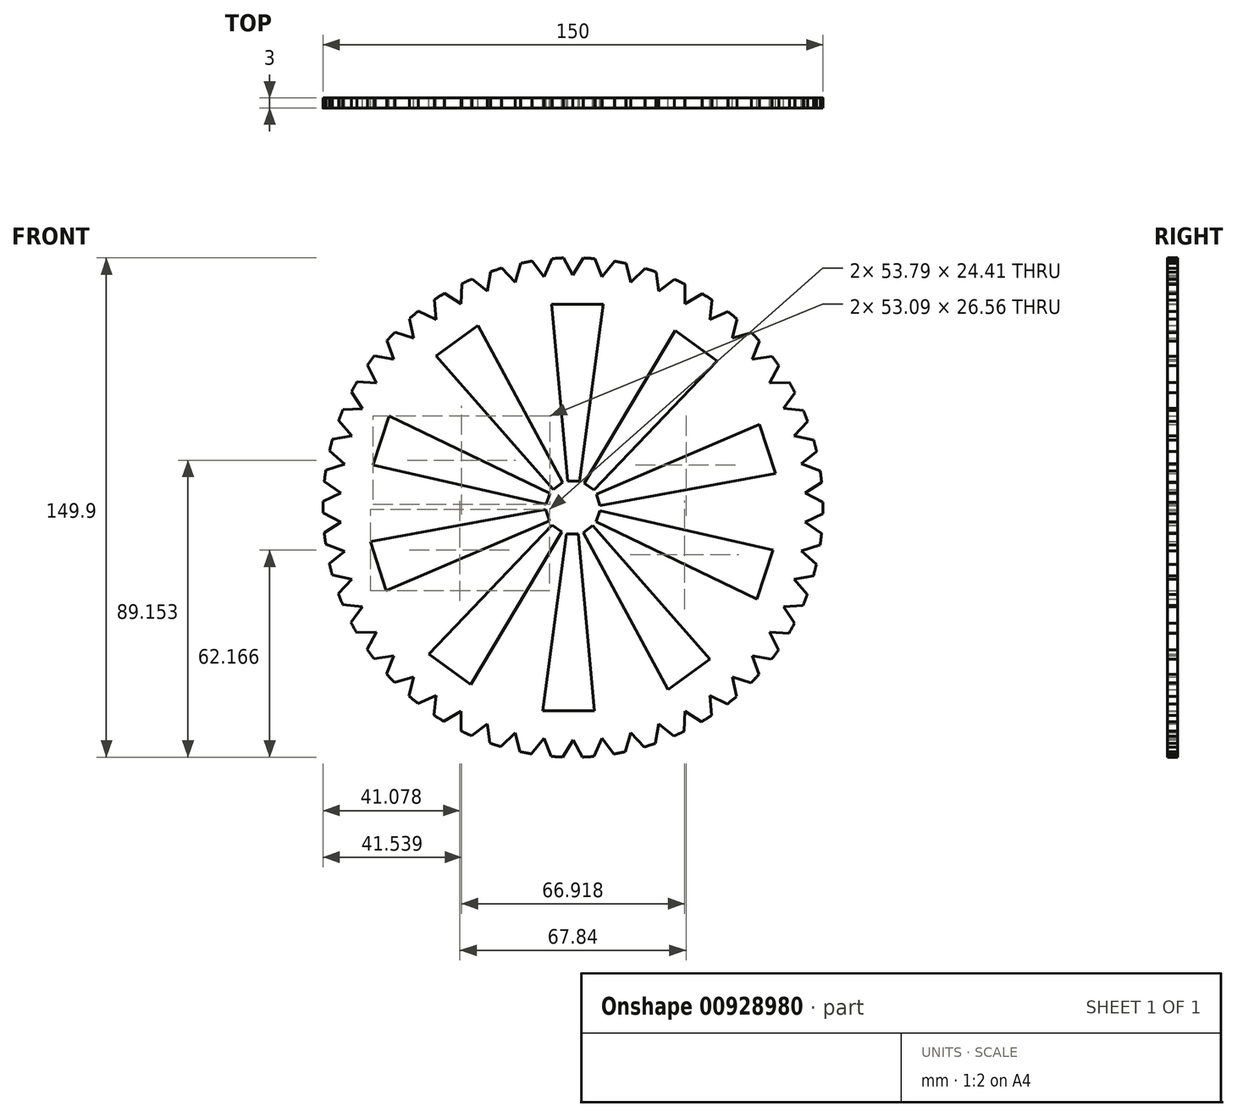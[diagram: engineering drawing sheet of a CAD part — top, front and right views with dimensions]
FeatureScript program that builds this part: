
annotation { "Feature Type Name" : "Feature", "Feature Type Description" : "" }
export const myFeature = defineFeature(function(context is Context, id is Id, definition is map)
    precondition{}
    {
        {
            var Q0;
            Q0=qCreatedBy(makeId("Front.planeOp"),FACE);
            var sketch = newSketch(context, id + "F0", { "sketchPlane" : qUnion([Q0])});
            skCircle(sketch, "E0", {"center": v(-17.07, 14.18) * mm, "radius": 75 * mm});
            skCircle(sketch, "E1.cCircle", {"center": v(-16.99, 88.46) * mm, "radius": 2.24 * mm, "construction": true});
            skLineSegment(sketch, "E1.0", {"start": v(-13.07, 90.62) * mm, "end": v(-17.08, 83.99) * mm});
            skLineSegment(sketch, "E1.1", {"start": v(-17.08, 83.99) * mm, "end": v(-20.82, 90.77) * mm});
            skLineSegment(sketch, "E1.2", {"start": v(-20.82, 90.77) * mm, "end": v(-13.07, 90.62) * mm});
            skPoint(sketch, "E1.0.midPoint", {"position": v(-15.07, 87.3) * mm});
            skPoint(sketch, "E2.1.0", {"position": v(-24.25, 86.98) * mm});
            skLineSegment(sketch, "E2.1.1", {"start": v(-30.39, 89.7) * mm, "end": v(-22.68, 90.52) * mm});
            skCircle(sketch, "E2.1.2", {"center": v(-26.3, 87.88) * mm, "radius": 2.24 * mm, "construction": true});
            skLineSegment(sketch, "E2.1.3", {"start": v(-22.68, 90.52) * mm, "end": v(-25.83, 83.43) * mm});
            skLineSegment(sketch, "E2.1.4", {"start": v(-25.83, 83.43) * mm, "end": v(-30.39, 89.7) * mm});
            skPoint(sketch, "E2.2.0", {"position": v(-33.32, 85.5) * mm});
            skLineSegment(sketch, "E2.2.1", {"start": v(-39.75, 87.44) * mm, "end": v(-32.2, 89.21) * mm});
            skCircle(sketch, "E2.2.2", {"center": v(-35.46, 86.15) * mm, "radius": 2.24 * mm, "construction": true});
            skLineSegment(sketch, "E2.2.3", {"start": v(-32.2, 89.21) * mm, "end": v(-34.44, 81.8) * mm});
            skLineSegment(sketch, "E2.2.4", {"start": v(-34.44, 81.8) * mm, "end": v(-39.75, 87.44) * mm});
            skPoint(sketch, "E2.3.0", {"position": v(-42.13, 82.9) * mm});
            skLineSegment(sketch, "E2.3.1", {"start": v(-48.75, 84.02) * mm, "end": v(-41.49, 86.73) * mm});
            skCircle(sketch, "E2.3.2", {"center": v(-44.34, 83.27) * mm, "radius": 2.24 * mm, "construction": true});
            skLineSegment(sketch, "E2.3.3", {"start": v(-41.49, 86.73) * mm, "end": v(-42.77, 79.08) * mm});
            skLineSegment(sketch, "E2.3.4", {"start": v(-42.77, 79.08) * mm, "end": v(-48.75, 84.02) * mm});
            skPoint(sketch, "E2.4.0", {"position": v(-50.55, 79.22) * mm});
            skLineSegment(sketch, "E2.4.1", {"start": v(-57.25, 79.5) * mm, "end": v(-50.39, 83.1) * mm});
            skCircle(sketch, "E2.4.2", {"center": v(-52.78, 79.31) * mm, "radius": 2.24 * mm, "construction": true});
            skLineSegment(sketch, "E2.4.3", {"start": v(-50.39, 83.1) * mm, "end": v(-50.7, 75.35) * mm});
            skLineSegment(sketch, "E2.4.4", {"start": v(-50.7, 75.35) * mm, "end": v(-57.25, 79.5) * mm});
            skPoint(sketch, "E2.5.0", {"position": v(-58.43, 74.51) * mm});
            skLineSegment(sketch, "E2.5.1", {"start": v(-65.12, 73.94) * mm, "end": v(-58.76, 78.37) * mm});
            skCircle(sketch, "E2.5.2", {"center": v(-60.66, 74.32) * mm, "radius": 2.24 * mm, "construction": true});
            skLineSegment(sketch, "E2.5.3", {"start": v(-58.76, 78.37) * mm, "end": v(-58.1, 70.65) * mm});
            skLineSegment(sketch, "E2.5.4", {"start": v(-58.1, 70.65) * mm, "end": v(-65.12, 73.94) * mm});
            skPoint(sketch, "E2.6.0", {"position": v(-65.67, 68.85) * mm});
            skLineSegment(sketch, "E2.6.1", {"start": v(-72.24, 67.45) * mm, "end": v(-66.48, 72.64) * mm});
            skCircle(sketch, "E2.6.2", {"center": v(-67.86, 68.38) * mm, "radius": 2.24 * mm, "construction": true});
            skLineSegment(sketch, "E2.6.3", {"start": v(-66.48, 72.64) * mm, "end": v(-64.86, 65.06) * mm});
            skLineSegment(sketch, "E2.6.4", {"start": v(-64.86, 65.06) * mm, "end": v(-72.24, 67.45) * mm});
            skPoint(sketch, "E2.7.0", {"position": v(-72.14, 62.33) * mm});
            skLineSegment(sketch, "E2.7.1", {"start": v(-78.48, 60.12) * mm, "end": v(-73.42, 65.99) * mm});
            skCircle(sketch, "E2.7.2", {"center": v(-74.25, 61.6) * mm, "radius": 2.24 * mm, "construction": true});
            skLineSegment(sketch, "E2.7.3", {"start": v(-73.42, 65.99) * mm, "end": v(-70.86, 58.67) * mm});
            skLineSegment(sketch, "E2.7.4", {"start": v(-70.86, 58.67) * mm, "end": v(-78.48, 60.12) * mm});
            skPoint(sketch, "E2.8.0", {"position": v(-77.74, 55.05) * mm});
            skLineSegment(sketch, "E2.8.1", {"start": v(-83.75, 52.06) * mm, "end": v(-79.47, 58.52) * mm});
            skCircle(sketch, "E2.8.2", {"center": v(-79.74, 54.05) * mm, "radius": 2.24 * mm, "construction": true});
            skLineSegment(sketch, "E2.8.3", {"start": v(-79.47, 58.52) * mm, "end": v(-76.01, 51.58) * mm});
            skLineSegment(sketch, "E2.8.4", {"start": v(-76.01, 51.58) * mm, "end": v(-83.75, 52.06) * mm});
            skPoint(sketch, "E2.9.0", {"position": v(-82.38, 47.12) * mm});
            skLineSegment(sketch, "E2.9.1", {"start": v(-87.97, 43.4) * mm, "end": v(-84.53, 50.35) * mm});
            skCircle(sketch, "E2.9.2", {"center": v(-84.25, 45.88) * mm, "radius": 2.24 * mm, "construction": true});
            skLineSegment(sketch, "E2.9.3", {"start": v(-84.53, 50.35) * mm, "end": v(-80.23, 43.9) * mm});
            skLineSegment(sketch, "E2.9.4", {"start": v(-80.23, 43.9) * mm, "end": v(-87.97, 43.4) * mm});
            skPoint(sketch, "E2.10.0", {"position": v(-86, 38.68) * mm});
            skLineSegment(sketch, "E2.10.1", {"start": v(-91.07, 34.29) * mm, "end": v(-88.53, 41.6) * mm});
            skCircle(sketch, "E2.10.2", {"center": v(-87.69, 37.21) * mm, "radius": 2.24 * mm, "construction": true});
            skLineSegment(sketch, "E2.10.3", {"start": v(-88.53, 41.6) * mm, "end": v(-83.46, 35.75) * mm});
            skLineSegment(sketch, "E2.10.4", {"start": v(-83.46, 35.75) * mm, "end": v(-91.07, 34.29) * mm});
            skPoint(sketch, "E2.11.0", {"position": v(-88.52, 29.85) * mm});
            skLineSegment(sketch, "E2.11.1", {"start": v(-93.01, 24.85) * mm, "end": v(-91.4, 32.44) * mm});
            skCircle(sketch, "E2.11.2", {"center": v(-90.02, 28.18) * mm, "radius": 2.24 * mm, "construction": true});
            skLineSegment(sketch, "E2.11.3", {"start": v(-91.4, 32.44) * mm, "end": v(-85.64, 27.26) * mm});
            skLineSegment(sketch, "E2.11.4", {"start": v(-85.64, 27.26) * mm, "end": v(-93.01, 24.85) * mm});
            skPoint(sketch, "E2.12.0", {"position": v(-89.92, 20.77) * mm});
            skLineSegment(sketch, "E2.12.1", {"start": v(-93.75, 15.25) * mm, "end": v(-93.1, 22.98) * mm});
            skCircle(sketch, "E2.12.2", {"center": v(-91.2, 18.93) * mm, "radius": 2.24 * mm, "construction": true});
            skLineSegment(sketch, "E2.12.3", {"start": v(-93.1, 22.98) * mm, "end": v(-86.74, 18.56) * mm});
            skLineSegment(sketch, "E2.12.4", {"start": v(-86.74, 18.56) * mm, "end": v(-93.75, 15.25) * mm});
            skPoint(sketch, "E2.13.0", {"position": v(-90.18, 11.58) * mm});
            skLineSegment(sketch, "E2.13.1", {"start": v(-93.28, 5.63) * mm, "end": v(-93.61, 13.38) * mm});
            skCircle(sketch, "E2.13.2", {"center": v(-91.2, 9.6) * mm, "radius": 2.24 * mm, "construction": true});
            skLineSegment(sketch, "E2.13.3", {"start": v(-93.61, 13.38) * mm, "end": v(-86.74, 9.8) * mm});
            skLineSegment(sketch, "E2.13.4", {"start": v(-86.74, 9.8) * mm, "end": v(-93.28, 5.63) * mm});
            skPoint(sketch, "E2.14.0", {"position": v(-89.27, 2.44) * mm});
            skLineSegment(sketch, "E2.14.1", {"start": v(-91.6, -3.85) * mm, "end": v(-92.9, 3.79) * mm});
            skCircle(sketch, "E2.14.2", {"center": v(-90.05, 0.34) * mm, "radius": 2.24 * mm, "construction": true});
            skLineSegment(sketch, "E2.14.3", {"start": v(-92.9, 3.79) * mm, "end": v(-85.64, 1.1) * mm});
            skLineSegment(sketch, "E2.14.4", {"start": v(-85.64, 1.1) * mm, "end": v(-91.6, -3.85) * mm});
            skPoint(sketch, "E2.15.0", {"position": v(-87.23, -6.51) * mm});
            skLineSegment(sketch, "E2.15.1", {"start": v(-88.76, -13.05) * mm, "end": v(-91, -5.63) * mm});
            skCircle(sketch, "E2.15.2", {"center": v(-87.74, -8.7) * mm, "radius": 2.24 * mm, "construction": true});
            skLineSegment(sketch, "E2.15.3", {"start": v(-91, -5.63) * mm, "end": v(-83.46, -7.4) * mm});
            skLineSegment(sketch, "E2.15.4", {"start": v(-83.46, -7.4) * mm, "end": v(-88.76, -13.05) * mm});
            skPoint(sketch, "E2.16.0", {"position": v(-84.09, -15.14) * mm});
            skLineSegment(sketch, "E2.16.1", {"start": v(-84.78, -21.82) * mm, "end": v(-87.94, -14.74) * mm});
            skCircle(sketch, "E2.16.2", {"center": v(-84.32, -17.37) * mm, "radius": 2.24 * mm, "construction": true});
            skLineSegment(sketch, "E2.16.3", {"start": v(-87.94, -14.74) * mm, "end": v(-80.23, -15.55) * mm});
            skLineSegment(sketch, "E2.16.4", {"start": v(-80.23, -15.55) * mm, "end": v(-84.78, -21.82) * mm});
            skPoint(sketch, "E2.17.0", {"position": v(-79.88, -23.31) * mm});
            skLineSegment(sketch, "E2.17.1", {"start": v(-79.73, -30.02) * mm, "end": v(-83.76, -23.4) * mm});
            skCircle(sketch, "E2.17.2", {"center": v(-79.83, -25.55) * mm, "radius": 2.24 * mm, "construction": true});
            skLineSegment(sketch, "E2.17.3", {"start": v(-83.76, -23.4) * mm, "end": v(-76, -23.23) * mm});
            skLineSegment(sketch, "E2.17.4", {"start": v(-76, -23.23) * mm, "end": v(-79.73, -30.02) * mm});
            skPoint(sketch, "E2.18.0", {"position": v(-74.69, -30.89) * mm});
            skLineSegment(sketch, "E2.18.1", {"start": v(-73.7, -37.53) * mm, "end": v(-78.52, -31.46) * mm});
            skCircle(sketch, "E2.18.2", {"center": v(-74.36, -33.1) * mm, "radius": 2.24 * mm, "construction": true});
            skLineSegment(sketch, "E2.18.3", {"start": v(-78.52, -31.46) * mm, "end": v(-70.85, -30.32) * mm});
            skLineSegment(sketch, "E2.18.4", {"start": v(-70.85, -30.32) * mm, "end": v(-73.7, -37.53) * mm});
            skPoint(sketch, "E2.19.0", {"position": v(-68.58, -37.75) * mm});
            skLineSegment(sketch, "E2.19.1", {"start": v(-66.77, -44.22) * mm, "end": v(-72.32, -38.8) * mm});
            skCircle(sketch, "E2.19.2", {"center": v(-67.98, -39.9) * mm, "radius": 2.24 * mm, "construction": true});
            skLineSegment(sketch, "E2.19.3", {"start": v(-72.32, -38.8) * mm, "end": v(-64.85, -36.7) * mm});
            skLineSegment(sketch, "E2.19.4", {"start": v(-64.85, -36.7) * mm, "end": v(-66.77, -44.22) * mm});
            skPoint(sketch, "E2.20.0", {"position": v(-61.67, -43.8) * mm});
            skLineSegment(sketch, "E2.20.1", {"start": v(-59.06, -49.99) * mm, "end": v(-65.24, -45.3) * mm});
            skCircle(sketch, "E2.20.2", {"center": v(-60.8, -45.86) * mm, "radius": 2.24 * mm, "construction": true});
            skLineSegment(sketch, "E2.20.3", {"start": v(-65.24, -45.3) * mm, "end": v(-58.1, -42.3) * mm});
            skLineSegment(sketch, "E2.20.4", {"start": v(-58.1, -42.3) * mm, "end": v(-59.06, -49.99) * mm});
            skPoint(sketch, "E2.21.0", {"position": v(-54.05, -48.93) * mm});
            skLineSegment(sketch, "E2.21.1", {"start": v(-50.69, -54.74) * mm, "end": v(-57.4, -50.88) * mm});
            skCircle(sketch, "E2.21.2", {"center": v(-52.93, -50.87) * mm, "radius": 2.24 * mm, "construction": true});
            skLineSegment(sketch, "E2.21.3", {"start": v(-57.4, -50.88) * mm, "end": v(-50.7, -47) * mm});
            skLineSegment(sketch, "E2.21.4", {"start": v(-50.7, -47) * mm, "end": v(-50.69, -54.74) * mm});
            skPoint(sketch, "E2.22.0", {"position": v(-45.85, -53.07) * mm});
            skLineSegment(sketch, "E2.22.1", {"start": v(-41.78, -58.41) * mm, "end": v(-48.93, -55.42) * mm});
            skCircle(sketch, "E2.22.2", {"center": v(-44.5, -54.85) * mm, "radius": 2.24 * mm, "construction": true});
            skLineSegment(sketch, "E2.22.3", {"start": v(-48.93, -55.42) * mm, "end": v(-42.76, -50.72) * mm});
            skLineSegment(sketch, "E2.22.4", {"start": v(-42.76, -50.72) * mm, "end": v(-41.78, -58.41) * mm});
            skPoint(sketch, "E2.23.0", {"position": v(-37.2, -56.15) * mm});
            skLineSegment(sketch, "E2.23.1", {"start": v(-32.49, -60.94) * mm, "end": v(-39.96, -58.86) * mm});
            skCircle(sketch, "E2.23.2", {"center": v(-35.63, -57.74) * mm, "radius": 2.24 * mm, "construction": true});
            skLineSegment(sketch, "E2.23.3", {"start": v(-39.96, -58.86) * mm, "end": v(-34.43, -53.43) * mm});
            skLineSegment(sketch, "E2.23.4", {"start": v(-34.43, -53.43) * mm, "end": v(-32.49, -60.94) * mm});
            skPoint(sketch, "E2.24.0", {"position": v(-28.22, -58.11) * mm});
            skLineSegment(sketch, "E2.24.1", {"start": v(-22.95, -62.28) * mm, "end": v(-30.62, -61.15) * mm});
            skCircle(sketch, "E2.24.2", {"center": v(-26.46, -59.5) * mm, "radius": 2.24 * mm, "construction": true});
            skLineSegment(sketch, "E2.24.3", {"start": v(-30.62, -61.15) * mm, "end": v(-25.82, -55.07) * mm});
            skLineSegment(sketch, "E2.24.4", {"start": v(-25.82, -55.07) * mm, "end": v(-22.95, -62.28) * mm});
            skPoint(sketch, "E2.25.0", {"position": v(-19.07, -58.94) * mm});
            skLineSegment(sketch, "E2.25.1", {"start": v(-13.32, -62.41) * mm, "end": v(-21.07, -62.26) * mm});
            skCircle(sketch, "E2.25.2", {"center": v(-17.16, -60.1) * mm, "radius": 2.24 * mm, "construction": true});
            skLineSegment(sketch, "E2.25.3", {"start": v(-21.07, -62.26) * mm, "end": v(-17.07, -55.62) * mm});
            skLineSegment(sketch, "E2.25.4", {"start": v(-17.07, -55.62) * mm, "end": v(-13.32, -62.41) * mm});
            skPoint(sketch, "E2.26.0", {"position": v(-9.9, -58.62) * mm});
            skLineSegment(sketch, "E2.26.1", {"start": v(-3.75, -61.34) * mm, "end": v(-11.46, -62.16) * mm});
            skCircle(sketch, "E2.26.2", {"center": v(-7.84, -59.52) * mm, "radius": 2.24 * mm, "construction": true});
            skLineSegment(sketch, "E2.26.3", {"start": v(-11.46, -62.16) * mm, "end": v(-8.32, -55.07) * mm});
            skLineSegment(sketch, "E2.26.4", {"start": v(-8.32, -55.07) * mm, "end": v(-3.75, -61.34) * mm});
            skPoint(sketch, "E2.27.0", {"position": v(-0.82, -57.14) * mm});
            skLineSegment(sketch, "E2.27.1", {"start": v(5.6, -59.07) * mm, "end": v(-1.94, -60.85) * mm});
            skCircle(sketch, "E2.27.2", {"center": v(1.32, -57.79) * mm, "radius": 2.24 * mm, "construction": true});
            skLineSegment(sketch, "E2.27.3", {"start": v(-1.94, -60.85) * mm, "end": v(0.3, -53.43) * mm});
            skLineSegment(sketch, "E2.27.4", {"start": v(0.3, -53.43) * mm, "end": v(5.6, -59.07) * mm});
            skPoint(sketch, "E2.28.0", {"position": v(7.99, -54.54) * mm});
            skLineSegment(sketch, "E2.28.1", {"start": v(14.6, -55.65) * mm, "end": v(7.35, -58.37) * mm});
            skCircle(sketch, "E2.28.2", {"center": v(10.2, -54.91) * mm, "radius": 2.24 * mm, "construction": true});
            skLineSegment(sketch, "E2.28.3", {"start": v(7.35, -58.37) * mm, "end": v(8.63, -50.72) * mm});
            skLineSegment(sketch, "E2.28.4", {"start": v(8.63, -50.72) * mm, "end": v(14.6, -55.65) * mm});
            skPoint(sketch, "E2.29.0", {"position": v(16.4, -50.86) * mm});
            skLineSegment(sketch, "E2.29.1", {"start": v(23.11, -51.13) * mm, "end": v(16.25, -54.73) * mm});
            skCircle(sketch, "E2.29.2", {"center": v(18.64, -50.95) * mm, "radius": 2.24 * mm, "construction": true});
            skLineSegment(sketch, "E2.29.3", {"start": v(16.25, -54.73) * mm, "end": v(16.56, -46.99) * mm});
            skLineSegment(sketch, "E2.29.4", {"start": v(16.56, -46.99) * mm, "end": v(23.11, -51.13) * mm});
            skPoint(sketch, "E2.30.0", {"position": v(24.3, -46.15) * mm});
            skLineSegment(sketch, "E2.30.1", {"start": v(30.98, -45.58) * mm, "end": v(24.62, -50.01) * mm});
            skCircle(sketch, "E2.30.2", {"center": v(26.52, -45.96) * mm, "radius": 2.24 * mm, "construction": true});
            skLineSegment(sketch, "E2.30.3", {"start": v(24.62, -50.01) * mm, "end": v(23.96, -42.29) * mm});
            skLineSegment(sketch, "E2.30.4", {"start": v(23.96, -42.29) * mm, "end": v(30.98, -45.58) * mm});
            skPoint(sketch, "E2.31.0", {"position": v(31.53, -40.5) * mm});
            skLineSegment(sketch, "E2.31.1", {"start": v(38.1, -39.09) * mm, "end": v(32.34, -44.28) * mm});
            skCircle(sketch, "E2.31.2", {"center": v(33.72, -40.02) * mm, "radius": 2.24 * mm, "construction": true});
            skLineSegment(sketch, "E2.31.3", {"start": v(32.34, -44.28) * mm, "end": v(30.72, -36.7) * mm});
            skLineSegment(sketch, "E2.31.4", {"start": v(30.72, -36.7) * mm, "end": v(38.1, -39.09) * mm});
            skPoint(sketch, "E2.32.0", {"position": v(38, -33.97) * mm});
            skLineSegment(sketch, "E2.32.1", {"start": v(44.33, -31.75) * mm, "end": v(39.27, -37.63) * mm});
            skCircle(sketch, "E2.32.2", {"center": v(40.1, -33.23) * mm, "radius": 2.24 * mm, "construction": true});
            skLineSegment(sketch, "E2.32.3", {"start": v(39.27, -37.63) * mm, "end": v(36.72, -30.31) * mm});
            skLineSegment(sketch, "E2.32.4", {"start": v(36.72, -30.31) * mm, "end": v(44.33, -31.75) * mm});
            skPoint(sketch, "E2.33.0", {"position": v(43.6, -26.69) * mm});
            skLineSegment(sketch, "E2.33.1", {"start": v(49.6, -23.7) * mm, "end": v(45.32, -30.16) * mm});
            skCircle(sketch, "E2.33.2", {"center": v(45.6, -25.7) * mm, "radius": 2.24 * mm, "construction": true});
            skLineSegment(sketch, "E2.33.3", {"start": v(45.32, -30.16) * mm, "end": v(41.87, -23.22) * mm});
            skLineSegment(sketch, "E2.33.4", {"start": v(41.87, -23.22) * mm, "end": v(49.6, -23.7) * mm});
            skPoint(sketch, "E2.34.0", {"position": v(48.24, -18.76) * mm});
            skLineSegment(sketch, "E2.34.1", {"start": v(53.83, -15.04) * mm, "end": v(50.39, -21.99) * mm});
            skCircle(sketch, "E2.34.2", {"center": v(50.1, -17.52) * mm, "radius": 2.24 * mm, "construction": true});
            skLineSegment(sketch, "E2.34.3", {"start": v(50.39, -21.99) * mm, "end": v(46.1, -15.54) * mm});
            skLineSegment(sketch, "E2.34.4", {"start": v(46.1, -15.54) * mm, "end": v(53.83, -15.04) * mm});
            skPoint(sketch, "E2.35.0", {"position": v(51.85, -10.32) * mm});
            skLineSegment(sketch, "E2.35.1", {"start": v(56.93, -5.92) * mm, "end": v(54.4, -13.25) * mm});
            skCircle(sketch, "E2.35.2", {"center": v(53.55, -8.85) * mm, "radius": 2.24 * mm, "construction": true});
            skLineSegment(sketch, "E2.35.3", {"start": v(54.4, -13.25) * mm, "end": v(49.32, -7.39) * mm});
            skLineSegment(sketch, "E2.35.4", {"start": v(49.32, -7.39) * mm, "end": v(56.93, -5.92) * mm});
            skPoint(sketch, "E2.36.0", {"position": v(54.38, -1.48) * mm});
            skLineSegment(sketch, "E2.36.1", {"start": v(58.87, 3.5) * mm, "end": v(57.26, -4.08) * mm});
            skCircle(sketch, "E2.36.2", {"center": v(55.88, 0.18) * mm, "radius": 2.24 * mm, "construction": true});
            skLineSegment(sketch, "E2.36.3", {"start": v(57.26, -4.08) * mm, "end": v(51.5, 1.1) * mm});
            skLineSegment(sketch, "E2.36.4", {"start": v(51.5, 1.1) * mm, "end": v(58.87, 3.5) * mm});
            skPoint(sketch, "E2.37.0", {"position": v(55.78, 7.6) * mm});
            skLineSegment(sketch, "E2.37.1", {"start": v(59.6, 13.11) * mm, "end": v(58.97, 5.39) * mm});
            skCircle(sketch, "E2.37.2", {"center": v(57.06, 9.43) * mm, "radius": 2.24 * mm, "construction": true});
            skLineSegment(sketch, "E2.37.3", {"start": v(58.97, 5.39) * mm, "end": v(52.6, 9.8) * mm});
            skLineSegment(sketch, "E2.37.4", {"start": v(52.6, 9.8) * mm, "end": v(59.6, 13.11) * mm});
            skPoint(sketch, "E2.38.0", {"position": v(56.03, 16.78) * mm});
            skLineSegment(sketch, "E2.38.1", {"start": v(59.14, 22.73) * mm, "end": v(59.47, 14.99) * mm});
            skCircle(sketch, "E2.38.2", {"center": v(57.07, 18.76) * mm, "radius": 2.24 * mm, "construction": true});
            skLineSegment(sketch, "E2.38.3", {"start": v(59.47, 14.99) * mm, "end": v(52.6, 18.57) * mm});
            skLineSegment(sketch, "E2.38.4", {"start": v(52.6, 18.57) * mm, "end": v(59.14, 22.73) * mm});
            skPoint(sketch, "E2.39.0", {"position": v(55.13, 25.92) * mm});
            skLineSegment(sketch, "E2.39.1", {"start": v(57.46, 32.21) * mm, "end": v(58.76, 24.57) * mm});
            skCircle(sketch, "E2.39.2", {"center": v(55.9, 28.02) * mm, "radius": 2.24 * mm, "construction": true});
            skLineSegment(sketch, "E2.39.3", {"start": v(58.76, 24.57) * mm, "end": v(51.5, 27.27) * mm});
            skLineSegment(sketch, "E2.39.4", {"start": v(51.5, 27.27) * mm, "end": v(57.46, 32.21) * mm});
            skPoint(sketch, "E2.40.0", {"position": v(53.09, 34.88) * mm});
            skLineSegment(sketch, "E2.40.1", {"start": v(54.61, 41.41) * mm, "end": v(56.86, 34) * mm});
            skCircle(sketch, "E2.40.2", {"center": v(53.6, 37.05) * mm, "radius": 2.24 * mm, "construction": true});
            skLineSegment(sketch, "E2.40.3", {"start": v(56.86, 34) * mm, "end": v(49.31, 35.76) * mm});
            skLineSegment(sketch, "E2.40.4", {"start": v(49.31, 35.76) * mm, "end": v(54.61, 41.41) * mm});
            skPoint(sketch, "E2.41.0", {"position": v(49.94, 43.5) * mm});
            skLineSegment(sketch, "E2.41.1", {"start": v(50.64, 50.18) * mm, "end": v(53.8, 43.1) * mm});
            skCircle(sketch, "E2.41.2", {"center": v(50.17, 45.73) * mm, "radius": 2.24 * mm, "construction": true});
            skLineSegment(sketch, "E2.41.3", {"start": v(53.8, 43.1) * mm, "end": v(46.09, 43.9) * mm});
            skLineSegment(sketch, "E2.41.4", {"start": v(46.09, 43.9) * mm, "end": v(50.64, 50.18) * mm});
            skPoint(sketch, "E2.42.0", {"position": v(45.74, 51.67) * mm});
            skLineSegment(sketch, "E2.42.1", {"start": v(45.6, 58.39) * mm, "end": v(49.61, 51.76) * mm});
            skCircle(sketch, "E2.42.2", {"center": v(45.69, 53.91) * mm, "radius": 2.24 * mm, "construction": true});
            skLineSegment(sketch, "E2.42.3", {"start": v(49.61, 51.76) * mm, "end": v(41.86, 51.59) * mm});
            skLineSegment(sketch, "E2.42.4", {"start": v(41.86, 51.59) * mm, "end": v(45.6, 58.39) * mm});
            skPoint(sketch, "E2.43.0", {"position": v(40.54, 59.25) * mm});
            skLineSegment(sketch, "E2.43.1", {"start": v(39.56, 65.9) * mm, "end": v(44.38, 59.82) * mm});
            skCircle(sketch, "E2.43.2", {"center": v(40.21, 61.46) * mm, "radius": 2.24 * mm, "construction": true});
            skLineSegment(sketch, "E2.43.3", {"start": v(44.38, 59.82) * mm, "end": v(36.71, 58.68) * mm});
            skLineSegment(sketch, "E2.43.4", {"start": v(36.71, 58.68) * mm, "end": v(39.56, 65.9) * mm});
            skPoint(sketch, "E2.44.0", {"position": v(34.44, 66.12) * mm});
            skLineSegment(sketch, "E2.44.1", {"start": v(32.63, 72.58) * mm, "end": v(38.17, 67.16) * mm});
            skCircle(sketch, "E2.44.2", {"center": v(33.84, 68.27) * mm, "radius": 2.24 * mm, "construction": true});
            skLineSegment(sketch, "E2.44.3", {"start": v(38.17, 67.16) * mm, "end": v(30.7, 65.07) * mm});
            skLineSegment(sketch, "E2.44.4", {"start": v(30.7, 65.07) * mm, "end": v(32.63, 72.58) * mm});
            skPoint(sketch, "E2.45.0", {"position": v(27.53, 72.16) * mm});
            skLineSegment(sketch, "E2.45.1", {"start": v(24.92, 78.35) * mm, "end": v(31.1, 73.67) * mm});
            skCircle(sketch, "E2.45.2", {"center": v(26.66, 74.22) * mm, "radius": 2.24 * mm, "construction": true});
            skLineSegment(sketch, "E2.45.3", {"start": v(31.1, 73.67) * mm, "end": v(23.95, 70.66) * mm});
            skLineSegment(sketch, "E2.45.4", {"start": v(23.95, 70.66) * mm, "end": v(24.92, 78.35) * mm});
            skPoint(sketch, "E2.46.0", {"position": v(19.9, 77.3) * mm});
            skLineSegment(sketch, "E2.46.1", {"start": v(16.54, 83.1) * mm, "end": v(23.26, 79.24) * mm});
            skCircle(sketch, "E2.46.2", {"center": v(18.79, 79.23) * mm, "radius": 2.24 * mm, "construction": true});
            skLineSegment(sketch, "E2.46.3", {"start": v(23.26, 79.24) * mm, "end": v(16.55, 75.35) * mm});
            skLineSegment(sketch, "E2.46.4", {"start": v(16.55, 75.35) * mm, "end": v(16.54, 83.1) * mm});
            skPoint(sketch, "E2.47.0", {"position": v(11.7, 81.43) * mm});
            skLineSegment(sketch, "E2.47.1", {"start": v(7.64, 86.77) * mm, "end": v(14.79, 83.78) * mm});
            skCircle(sketch, "E2.47.2", {"center": v(10.35, 83.21) * mm, "radius": 2.24 * mm, "construction": true});
            skLineSegment(sketch, "E2.47.3", {"start": v(14.79, 83.78) * mm, "end": v(8.62, 79.08) * mm});
            skLineSegment(sketch, "E2.47.4", {"start": v(8.62, 79.08) * mm, "end": v(7.64, 86.77) * mm});
            skPoint(sketch, "E2.48.0", {"position": v(3.05, 84.5) * mm});
            skLineSegment(sketch, "E2.48.1", {"start": v(-1.65, 89.3) * mm, "end": v(5.82, 87.22) * mm});
            skCircle(sketch, "E2.48.2", {"center": v(1.48, 86.1) * mm, "radius": 2.24 * mm, "construction": true});
            skLineSegment(sketch, "E2.48.3", {"start": v(5.82, 87.22) * mm, "end": v(0.28, 81.8) * mm});
            skLineSegment(sketch, "E2.48.4", {"start": v(0.28, 81.8) * mm, "end": v(-1.65, 89.3) * mm});
            skPoint(sketch, "E2.49.0", {"position": v(-5.92, 86.48) * mm});
            skLineSegment(sketch, "E2.49.1", {"start": v(-11.19, 90.64) * mm, "end": v(-3.52, 89.52) * mm});
            skCircle(sketch, "E2.49.2", {"center": v(-7.68, 87.86) * mm, "radius": 2.24 * mm, "construction": true});
            skLineSegment(sketch, "E2.49.3", {"start": v(-3.52, 89.52) * mm, "end": v(-8.33, 83.44) * mm});
            skLineSegment(sketch, "E2.49.4", {"start": v(-8.33, 83.44) * mm, "end": v(-11.19, 90.64) * mm});
            skLineSegment(sketch, "E3", {"start": v(-23.53, 75.17) * mm, "end": v(-8, 75.17) * mm});
            skLineSegment(sketch, "E4", {"start": v(-8, 75.17) * mm, "end": v(-15.11, 22.09) * mm});
            skLineSegment(sketch, "E5", {"start": v(-15.11, 22.09) * mm, "end": v(-18.67, 22.09) * mm});
            skLineSegment(sketch, "E6", {"start": v(-18.67, 22.09) * mm, "end": v(-23.53, 75.17) * mm});
            skLineSegment(sketch, "E7.1.0", {"start": v(-58.15, 59.73) * mm, "end": v(-45.58, 68.86) * mm});
            skLineSegment(sketch, "E7.1.1", {"start": v(-23.02, 19.64) * mm, "end": v(-58.15, 59.73) * mm});
            skLineSegment(sketch, "E7.1.2", {"start": v(-45.58, 68.86) * mm, "end": v(-20.13, 21.73) * mm});
            skLineSegment(sketch, "E7.1.3", {"start": v(-20.13, 21.73) * mm, "end": v(-23.02, 19.64) * mm});
            skLineSegment(sketch, "E7.2.0", {"start": v(-77.07, 26.89) * mm, "end": v(-72.27, 41.66) * mm});
            skLineSegment(sketch, "E7.2.1", {"start": v(-25.09, 15.1) * mm, "end": v(-77.07, 26.89) * mm});
            skLineSegment(sketch, "E7.2.2", {"start": v(-72.27, 41.66) * mm, "end": v(-23.99, 18.49) * mm});
            skLineSegment(sketch, "E7.2.3", {"start": v(-23.99, 18.49) * mm, "end": v(-25.09, 15.1) * mm});
            skLineSegment(sketch, "E7.3.0", {"start": v(-73.08, -10.8) * mm, "end": v(-77.89, 3.97) * mm});
            skLineSegment(sketch, "E7.3.1", {"start": v(-24.1, 10.21) * mm, "end": v(-73.08, -10.8) * mm});
            skLineSegment(sketch, "E7.3.2", {"start": v(-77.89, 3.97) * mm, "end": v(-25.2, 13.6) * mm});
            skLineSegment(sketch, "E7.3.3", {"start": v(-25.2, 13.6) * mm, "end": v(-24.1, 10.21) * mm});
            skLineSegment(sketch, "E7.4.0", {"start": v(-47.7, -38.96) * mm, "end": v(-60.27, -29.83) * mm});
            skLineSegment(sketch, "E7.4.1", {"start": v(-20.42, 6.84) * mm, "end": v(-47.7, -38.96) * mm});
            skLineSegment(sketch, "E7.4.2", {"start": v(-60.27, -29.83) * mm, "end": v(-23.3, 8.93) * mm});
            skLineSegment(sketch, "E7.4.3", {"start": v(-23.3, 8.93) * mm, "end": v(-20.42, 6.84) * mm});
            skLineSegment(sketch, "E7.5.0", {"start": v(-10.62, -46.81) * mm, "end": v(-26.15, -46.81) * mm});
            skLineSegment(sketch, "E7.5.1", {"start": v(-15.47, 6.27) * mm, "end": v(-10.62, -46.81) * mm});
            skLineSegment(sketch, "E7.5.2", {"start": v(-26.15, -46.81) * mm, "end": v(-19.03, 6.27) * mm});
            skLineSegment(sketch, "E7.5.3", {"start": v(-19.03, 6.27) * mm, "end": v(-15.47, 6.27) * mm});
            skLineSegment(sketch, "E7.6.0", {"start": v(24, -31.37) * mm, "end": v(11.43, -40.5) * mm});
            skLineSegment(sketch, "E7.6.1", {"start": v(-11.13, 8.72) * mm, "end": v(24, -31.37) * mm});
            skLineSegment(sketch, "E7.6.2", {"start": v(11.43, -40.5) * mm, "end": v(-14, 6.63) * mm});
            skLineSegment(sketch, "E7.6.3", {"start": v(-14, 6.63) * mm, "end": v(-11.13, 8.72) * mm});
            skLineSegment(sketch, "E7.7.0", {"start": v(42.93, 1.47) * mm, "end": v(38.13, -13.3) * mm});
            skLineSegment(sketch, "E7.7.1", {"start": v(-9.06, 13.26) * mm, "end": v(42.93, 1.47) * mm});
            skLineSegment(sketch, "E7.7.2", {"start": v(38.13, -13.3) * mm, "end": v(-10.16, 9.87) * mm});
            skLineSegment(sketch, "E7.7.3", {"start": v(-10.16, 9.87) * mm, "end": v(-9.06, 13.26) * mm});
            skLineSegment(sketch, "E7.8.0", {"start": v(38.94, 39.17) * mm, "end": v(43.74, 24.4) * mm});
            skLineSegment(sketch, "E7.8.1", {"start": v(-10.05, 18.15) * mm, "end": v(38.94, 39.17) * mm});
            skLineSegment(sketch, "E7.8.2", {"start": v(43.74, 24.4) * mm, "end": v(-8.95, 14.76) * mm});
            skLineSegment(sketch, "E7.8.3", {"start": v(-8.95, 14.76) * mm, "end": v(-10.05, 18.15) * mm});
            skLineSegment(sketch, "E7.9.0", {"start": v(13.56, 67.32) * mm, "end": v(26.13, 58.19) * mm});
            skLineSegment(sketch, "E7.9.1", {"start": v(-13.72, 21.52) * mm, "end": v(13.56, 67.32) * mm});
            skLineSegment(sketch, "E7.9.2", {"start": v(26.13, 58.19) * mm, "end": v(-10.84, 19.43) * mm});
            skLineSegment(sketch, "E7.9.3", {"start": v(-10.84, 19.43) * mm, "end": v(-13.72, 21.52) * mm});
            skSolve(sketch);
        }
        {
            var Q0;
            Q0=makeQuery(id+"F0.imprint","IMPRINT",FACE,{"disambiguationData":[TD([[makeQuery(id+"F0.imprint","IMPRINT",EDGE,{"derivedFrom":sQuery(id+"F0.wireOp",EDGE,"E0")}),1.0]])]});
            extrude(context, id + "F1", {"entities" : qUnion([Q0]), "depth" : 3 * mm, "offsetDistance" : 25 * mm});
        }
    });
